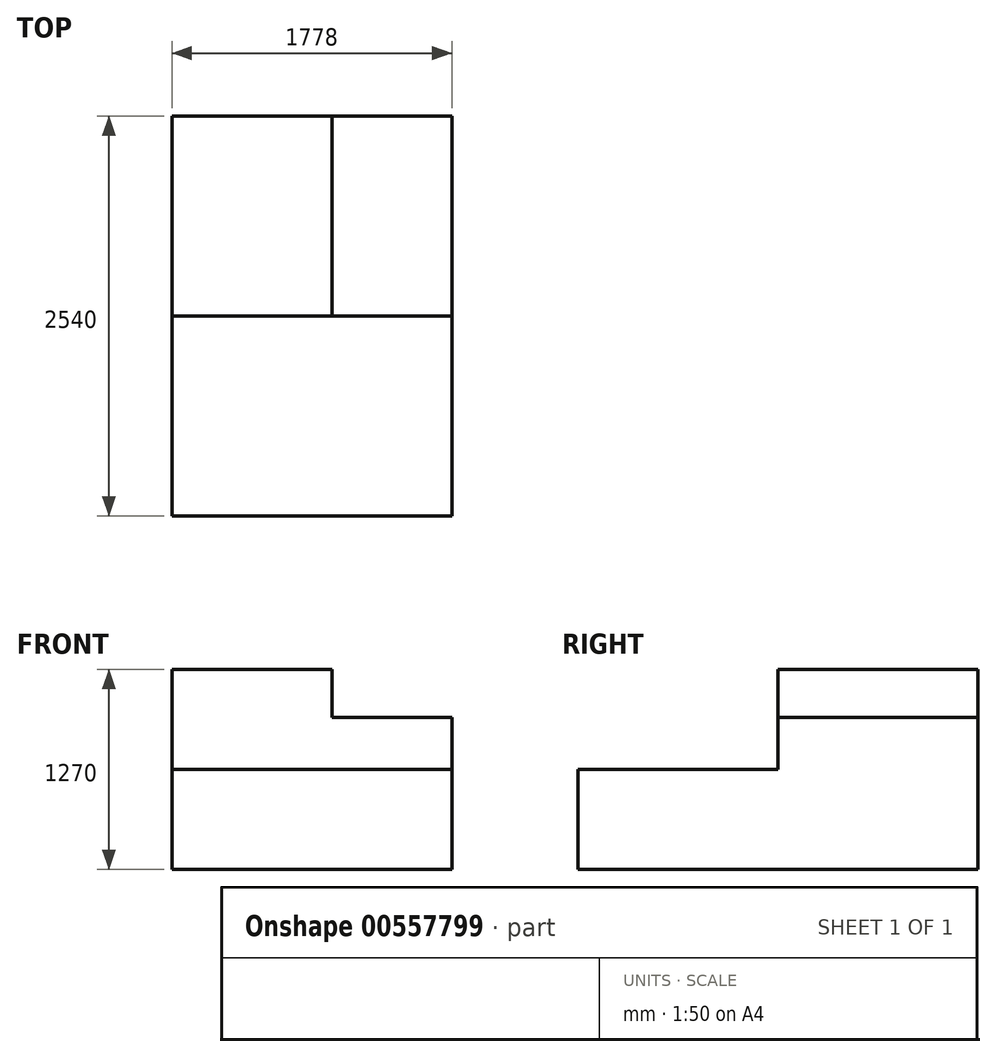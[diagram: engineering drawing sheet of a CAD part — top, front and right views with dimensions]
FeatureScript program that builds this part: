
annotation { "Feature Type Name" : "Feature", "Feature Type Description" : "" }
export const myFeature = defineFeature(function(context is Context, id is Id, definition is map)
    precondition{}
    {
        {
            var Q0;
            Q0=qCreatedBy(makeId("Front.planeOp"),FACE);
            var sketch = newSketch(context, id + "F0", { "sketchPlane" : qUnion([Q0])});
            skLineSegment(sketch, "E0", {"start": v(-135.38, -72.74) * mm, "end": v(-135.38, 562.26) * mm});
            skLineSegment(sketch, "E1", {"start": v(-135.38, 562.26) * mm, "end": v(1642.62, 562.26) * mm});
            skLineSegment(sketch, "E2", {"start": v(1642.62, 562.26) * mm, "end": v(1642.62, -72.74) * mm});
            skLineSegment(sketch, "E3", {"start": v(1642.62, -72.74) * mm, "end": v(-135.38, -72.74) * mm});
            skLineSegment(sketch, "E4", {"start": v(1642.62, 562.26) * mm, "end": v(1642.62, 892.46) * mm});
            skLineSegment(sketch, "E5", {"start": v(1642.62, 892.46) * mm, "end": v(880.62, 892.46) * mm});
            skLineSegment(sketch, "E6", {"start": v(880.62, 892.46) * mm, "end": v(880.62, 562.26) * mm});
            skLineSegment(sketch, "E7", {"start": v(880.62, 562.26) * mm, "end": v(880.62, 1197.26) * mm});
            skLineSegment(sketch, "E8", {"start": v(880.62, 1197.26) * mm, "end": v(-135.38, 1197.26) * mm});
            skLineSegment(sketch, "E9", {"start": v(-135.38, 1197.26) * mm, "end": v(-135.38, 562.26) * mm});
            skSolve(sketch);
        }
        {
            var Q0;
            {var subQ3=sQuery(id+"F0.wireOp",EDGE,"E0");Q0=makeQuery(id+"F0.imprint","IMPRINT",FACE,{"disambiguationData":[TD([[makeQuery(id+"F0.imprint","IMPRINT",EDGE,{"derivedFrom":subQ3}),-1.0]])]});}
            extrude(context, id + "F1", {"entities" : qUnion([Q0]), "depth" : 2540 * mm, "offsetDistance" : 25.4 * mm});
        }
        {
            var Q0;
            {var subQ0=sQuery(id+"F0.wireOp",EDGE,"E8");Q0=makeQuery(id+"F0.imprint","IMPRINT",FACE,{"disambiguationData":[TD([[makeQuery(id+"F0.imprint","IMPRINT",EDGE,{"derivedFrom":subQ0}),1.0]])]});}
            var Q1;
            {var subQ0=sQuery(id+"F0.wireOp",EDGE,"E4");Q1=makeQuery(id+"F0.imprint","IMPRINT",FACE,{"disambiguationData":[TD([[makeQuery(id+"F0.imprint","IMPRINT",EDGE,{"derivedFrom":subQ0}),1.0]])]});}
            extrude(context, id + "F2", {"entities" : qUnion([Q0, Q1]), "operationType" : NewBodyOperationType.ADD, "depth" : 1270 * mm, "offsetDistance" : 25.4 * mm});
        }
    });
